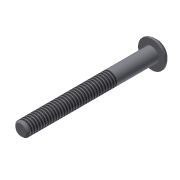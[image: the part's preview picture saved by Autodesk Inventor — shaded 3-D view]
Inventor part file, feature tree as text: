
AUTODESK INVENTOR PART (.ipt)
format: ipt  version: 2013 (Build 170138000, 138)  size: 122,368 bytes
history: native  units: in
note: dims shown in document units (in); Inventor stores cm internally (conversion verified against a paired STEP export)
features: sketch x3, extrude x2, revolve x1, chamfer x1, thread x1
ambient origin geometry x8: Origin, YZ Plane, XZ Plane, XY Plane, X Axis, Y Axis, Z Axis, Center Point
bodies: Solid1 (feature_tree)
feature tree (8):
  extrude  "Extrusion1"  Depth=1.5in TaperAngle=0.0deg
  revolve  "Revolution1"  [1 undecoded]
  extrude  "Extrusion2"  Depth=0.0938in
  chamfer  "Chamfer1"  Distance=0.0625in
  thread  "Thread1"  [1 undecoded]
  sketch  "Sketch1"  dims[d0=0.164in d1=1.5in d2=0.0in]
  sketch  "Sketch2"  dims[d3=0.087in d6=0.08in]
  sketch  "Sketch3"  dims[d7=90.0deg d8=0.0938in d9=0.0625in d10=0.0in d13=0.02in d14=0.125in d15=45.0deg d16=1.0in d17=0.0in d19=0.156in]
note: 2 required parameter values undecoded (feature->parameter linkage not recoverable at this tier; creation-order binding heuristic only, values carry confidence <= 0.55)